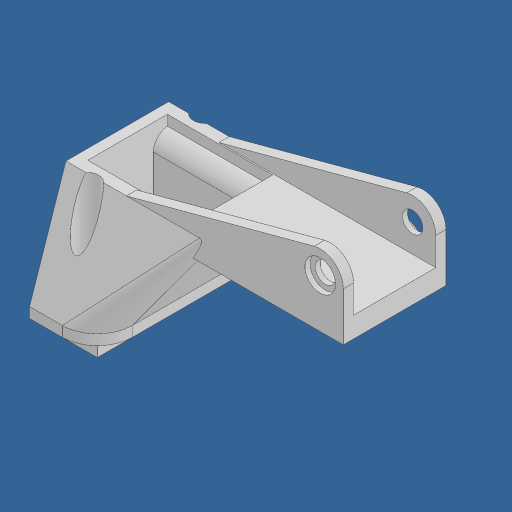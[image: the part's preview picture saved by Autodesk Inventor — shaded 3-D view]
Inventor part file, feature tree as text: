
AUTODESK INVENTOR PART (.ipt)
format: ipt  version: 2024.2 (Build 282272000, 272)  size: 259,584 bytes
history: native  units: mm
features: sketch x10, extrude x8, plane x1, loft x1, hole x1, mirror x1, fillet x1, other x1
ambient origin geometry x8: Origin, YZ Plane, XZ Plane, XY Plane, X Axis, Y Axis, Z Axis, Center Point
bodies: Solid1 (feature_tree)
feature tree (24):
  extrude  "Extrusion1"  Depth=30.2mm
  extrude  "Extrusion2"  Depth=2.0mm
  plane  "Work Plane1"
  loft  "Loft1"
  extrude  "Extrusion3"  Depth=25.0mm
  hole  "Hole1"  [1 undecoded]
  extrude  "Extrusion4"  TaperAngle=0.0deg  [1 undecoded]
  extrude  "Extrusion6"  Depth=2.0mm
  extrude  "Extrusion7"  Depth=10.0mm
  mirror  "Mirror1"
  fillet  "Fillet1"  Radius=10.0mm
  extrude  "Extrusion8"  Depth=11.5mm
  extrude  "Extrusion9"  Depth=1.0mm TaperAngle=0.0deg
  sketch  "Sketch1"  dims[d0=11.2mm d1=30.2mm]
  sketch  "Sketch2"  dims[d2=2.0mm d3=0.0mm d4=2.0mm]
  sketch  "Sketch3"  dims[d5=2.0mm d6=2.0mm]
  other  "Edges1"
  sketch  "Sketch4"  dims[d7=2.0mm d8=0.0mm d9=25.0mm]
  sketch  "Sketch5"  dims[d10=20.0mm d11=28.0mm]
  sketch  "Sketch6"  dims[d12=0.0mm d13=90.0deg d14=0.0mm d15=90.0deg]
  sketch  "Sketch8"  dims[d16=20.5mm d17=2.0mm]
  sketch  "Sketch10"  dims[d18=2.0mm d19=2.0mm d20=10.0mm d21=0.0mm]
  sketch  "Sketch11"  dims[d22=11.5mm d23=11.5mm]
  sketch  "Sketch12"  dims[d24=4.6mm d25=6.0mm d26=6.3mm d27=2.0mm d28=90.0deg d29=6.0mm d30=20.594885mm d32=2.0mm d33=0.0mm d44=4.0mm d45=20.0mm d46=0.0mm d47=54.0mm d48=4.0mm d49=5.45mm d50=4.5mm d51=4.5mm d52=2.0mm d53=0.0mm d57=15.0deg d58=6.8mm d59=2.0mm d60=45.0deg d61=15.5mm d62=3.0mm d63=45.0deg d64=24.5mm d65=6.0mm d66=1.0mm d67=0.0mm d68=6.0mm d69=1.0mm d70=0.0mm]
note: 2 required parameter values undecoded (feature->parameter linkage not recoverable at this tier; creation-order binding heuristic only, values carry confidence <= 0.55)
